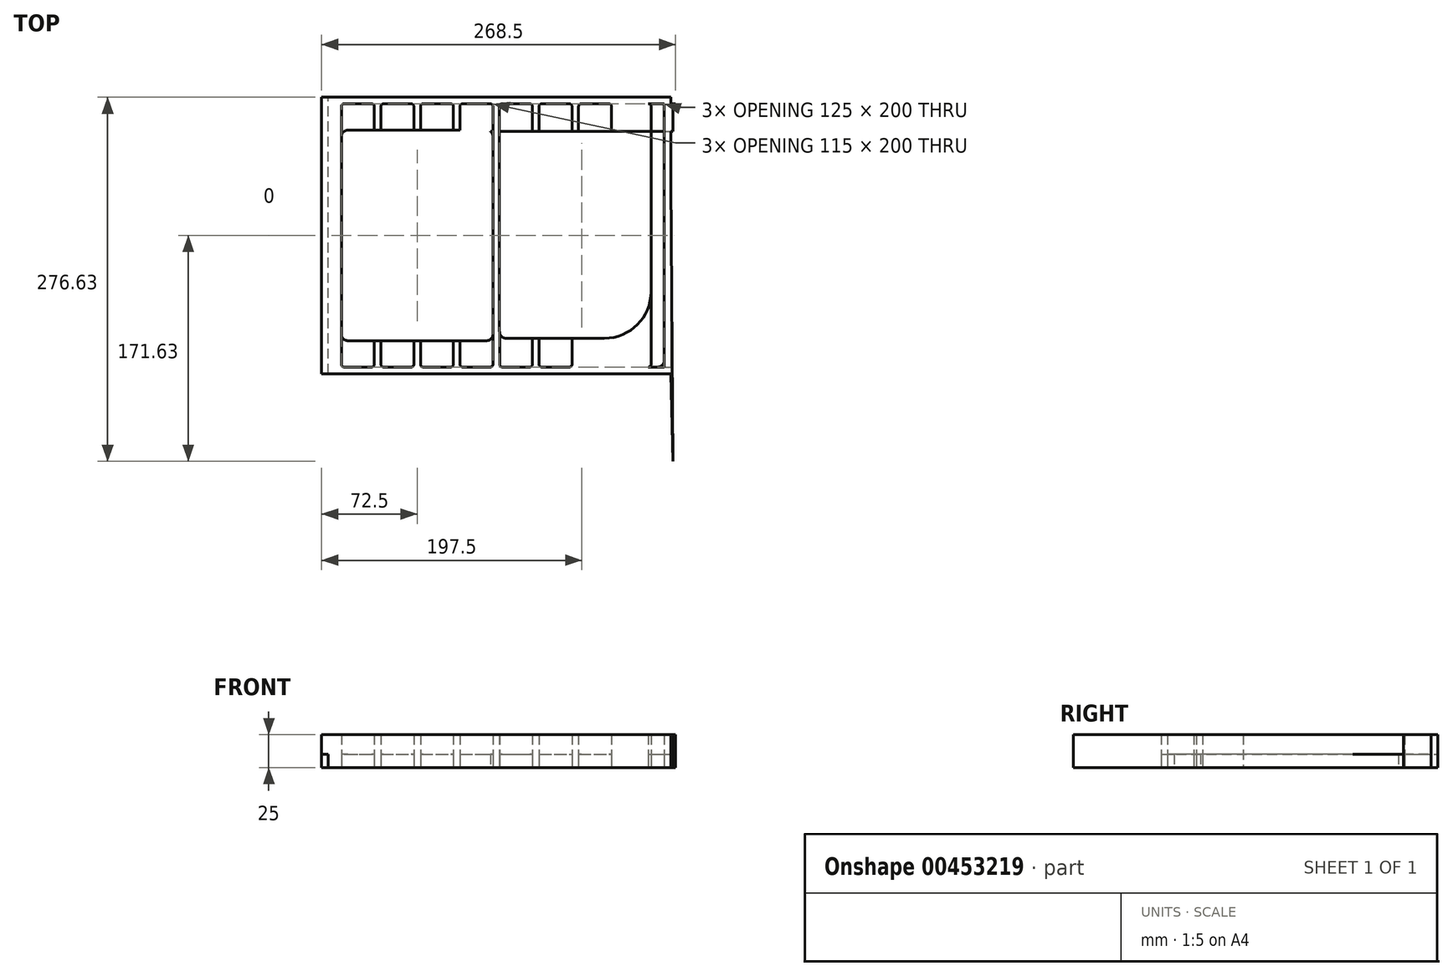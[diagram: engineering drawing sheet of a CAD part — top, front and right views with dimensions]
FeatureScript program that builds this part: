
annotation { "Feature Type Name" : "Feature", "Feature Type Description" : "" }
export const myFeature = defineFeature(function(context is Context, id is Id, definition is map)
    precondition{}
    {
        {
            var Q0;
            Q0=qCreatedBy(makeId("Top.planeOp"),FACE);
            var sketch = newSketch(context, id + "F0", { "sketchPlane" : qUnion([Q0])});
            skLineSegment(sketch, "E0.bottom", {"start": v(132.5, 105) * mm, "end": v(-132.5, 105) * mm});
            skLineSegment(sketch, "E0.top", {"start": v(132.5, -105) * mm, "end": v(-132.5, -105) * mm});
            skLineSegment(sketch, "E0.left", {"start": v(132.5, 105) * mm, "end": v(132.5, -105) * mm});
            skLineSegment(sketch, "E0.right", {"start": v(-132.5, 105) * mm, "end": v(-132.5, -105) * mm});
            skPoint(sketch, "E0.middle", {"position": v(0, 0) * mm});
            skLineSegment(sketch, "E1", {"start": v(-127.5, 95) * mm, "end": v(-127.5, -95) * mm});
            skLineSegment(sketch, "E2", {"start": v(0, 111.23) * mm, "end": v(0, -100) * mm, "construction": true});
            skPoint(sketch, "E2.endSnap0", {"position": v(0, -105) * mm});
            skLineSegment(sketch, "E3", {"start": v(-62.5, -80) * mm, "end": v(-62.5, -98) * mm});
            skLineSegment(sketch, "E4", {"start": v(-2.5, 75) * mm, "end": v(-2.5, -75) * mm});
            skLineSegment(sketch, "E5", {"start": v(2.5, 107.2) * mm, "end": v(2.5, -73.12) * mm});
            skLineSegment(sketch, "E6", {"start": v(-117.5, 75) * mm, "end": v(-117.5, -75) * mm});
            skLineSegment(sketch, "E7", {"start": v(27.5, 98) * mm, "end": v(27.5, 78.96) * mm});
            skLineSegment(sketch, "E8", {"start": v(57.5, 98) * mm, "end": v(57.5, 78.96) * mm});
            skLineSegment(sketch, "E9", {"start": v(87.5, 98) * mm, "end": v(87.5, 78.96) * mm});
            skLineSegment(sketch, "E10", {"start": v(117.5, 107.2) * mm, "end": v(117.5, -42.8) * mm});
            skLineSegment(sketch, "E11", {"start": v(32.5, 98) * mm, "end": v(32.5, 78.96) * mm});
            skLineSegment(sketch, "E12", {"start": v(62.5, 98) * mm, "end": v(62.5, 78.96) * mm});
            skLineSegment(sketch, "E13", {"start": v(134, 98) * mm, "end": v(134, 78.96) * mm});
            skLineSegment(sketch, "E14", {"start": v(127.5, 95) * mm, "end": v(127.5, -95) * mm});
            skLineSegment(sketch, "E15", {"start": v(-85.5, 100) * mm, "end": v(-64.5, 100) * mm});
            skLineSegment(sketch, "E16", {"start": v(-112.5, 80) * mm, "end": v(-7.5, 80) * mm});
            skLineSegment(sketch, "E17", {"start": v(-25.74, 78.96) * mm, "end": v(134, 78.96) * mm});
            skLineSegment(sketch, "E18", {"start": v(115.5, -100) * mm, "end": v(136, -100) * mm});
            skLineSegment(sketch, "E19", {"start": v(-112.5, -80) * mm, "end": v(-7.5, -80) * mm});
            skLineSegment(sketch, "E20", {"start": v(7.5, -78.12) * mm, "end": v(82.17, -78.12) * mm});
            skArc(sketch, "E21.filletArc", {"start": v(-112.5, 80) * mm, "mid": v(-116.04, 78.54) * mm, "end": v(-117.5, 75) * mm});
            skArc(sketch, "E22.filletArc", {"start": v(-117.5, -75) * mm, "mid": v(-116.04, -78.54) * mm, "end": v(-112.5, -80) * mm});
            skPoint(sketch, "E23.newPointB", {"position": v(-2.5, -72.8) * mm});
            skArc(sketch, "E23.filletArc", {"start": v(-7.5, -80) * mm, "mid": v(-3.96, -78.54) * mm, "end": v(-2.5, -75) * mm});
            skPoint(sketch, "E24.newPointB", {"position": v(-2.5, 137.2) * mm});
            skArc(sketch, "E24.filletArc", {"start": v(-2.5, 75) * mm, "mid": v(-3.96, 78.54) * mm, "end": v(-7.5, 80) * mm});
            skArc(sketch, "E25.filletArc", {"start": v(-25.74, 78.96) * mm, "mid": v(-29.57, 79.22) * mm, "end": v(-33.33, 80) * mm});
            skArc(sketch, "E26.filletArc", {"start": v(2.5, -73.12) * mm, "mid": v(3.96, -76.66) * mm, "end": v(7.5, -78.12) * mm});
            skArc(sketch, "E27.filletArc", {"start": v(82.17, -78.12) * mm, "mid": v(107.15, -67.77) * mm, "end": v(117.5, -42.8) * mm});
            skLineSegment(sketch, "E28.trimOffspring", {"start": v(-92.5, -80) * mm, "end": v(-92.5, -98) * mm});
            skLineSegment(sketch, "E29.trimOffspring", {"start": v(-87.5, -80) * mm, "end": v(-87.5, -98) * mm});
            skLineSegment(sketch, "E30.trimOffspring", {"start": v(-57.5, -80) * mm, "end": v(-57.5, -98) * mm});
            skLineSegment(sketch, "E31.trimOffspring", {"start": v(-32.5, -80) * mm, "end": v(-32.5, -98) * mm});
            skLineSegment(sketch, "E32.trimOffspring", {"start": v(-27.5, -80) * mm, "end": v(-27.5, -98) * mm});
            skLineSegment(sketch, "E33", {"start": v(-117.5, 100) * mm, "end": v(-122.5, 100) * mm});
            skLineSegment(sketch, "E34.trimOffspring", {"start": v(27.5, -78.12) * mm, "end": v(27.5, -98) * mm});
            skLineSegment(sketch, "E35.trimOffspring", {"start": v(32.5, -78.12) * mm, "end": v(32.5, -98) * mm});
            skLineSegment(sketch, "E36.trimOffspring", {"start": v(57.5, -78.12) * mm, "end": v(57.5, -98) * mm});
            skLineSegment(sketch, "E37.trimOffspring", {"start": v(62.5, -78.12) * mm, "end": v(62.5, -98) * mm});
            skLineSegment(sketch, "E38.trimOffspring", {"start": v(87.5, -78.12) * mm, "end": v(87.5, -98) * mm});
            skLineSegment(sketch, "E39.trimOffspring", {"start": v(134, -78.12) * mm, "end": v(134, -98) * mm});
            skLineSegment(sketch, "E40", {"start": v(-117.5, -100) * mm, "end": v(-122.5, -100) * mm});
            skLineSegment(sketch, "E41", {"start": v(117.5, -100) * mm, "end": v(122.5, -100) * mm});
            skLineSegment(sketch, "E42", {"start": v(117.5, 100) * mm, "end": v(122.5, 100) * mm});
            skLineSegment(sketch, "E43", {"start": v(2.5, 98) * mm, "end": v(2.5, 107.2) * mm});
            skLineSegment(sketch, "E44", {"start": v(-2.5, 75) * mm, "end": v(-2.5, 98) * mm});
            skLineSegment(sketch, "E45", {"start": v(-117.5, 75) * mm, "end": v(-117.5, 98) * mm});
            skLineSegment(sketch, "E46", {"start": v(-117.5, -75) * mm, "end": v(-117.5, -98) * mm});
            skLineSegment(sketch, "E47", {"start": v(-92.5, 98) * mm, "end": v(-92.5, 80) * mm});
            skLineSegment(sketch, "E48", {"start": v(-87.5, 98) * mm, "end": v(-87.5, 80) * mm});
            skLineSegment(sketch, "E49", {"start": v(-62.5, 98) * mm, "end": v(-62.5, 80) * mm});
            skLineSegment(sketch, "E50", {"start": v(-57.5, 98) * mm, "end": v(-57.5, 80) * mm});
            skLineSegment(sketch, "E51", {"start": v(-32.5, 98) * mm, "end": v(-32.5, 80) * mm});
            skLineSegment(sketch, "E52", {"start": v(-27.5, 98) * mm, "end": v(-27.5, 80) * mm});
            skLineSegment(sketch, "E53", {"start": v(117.5, 98) * mm, "end": v(117.5, 107.2) * mm});
            skLineSegment(sketch, "E54", {"start": v(117.5, -42.8) * mm, "end": v(117.5, -98) * mm});
            skPoint(sketch, "E55.visualSharp", {"position": v(-117.5, 100) * mm});
            skArc(sketch, "E55.filletArc", {"start": v(-115.5, 100) * mm, "mid": v(-116.91, 99.41) * mm, "end": v(-117.5, 98) * mm});
            skArc(sketch, "E56.filletArc", {"start": v(-127.5, -95) * mm, "mid": v(-126.04, -98.54) * mm, "end": v(-122.5, -100) * mm});
            skArc(sketch, "E57.filletArc", {"start": v(-122.5, 100) * mm, "mid": v(-126.04, 98.54) * mm, "end": v(-127.5, 95) * mm});
            skArc(sketch, "E58.filletArc", {"start": v(-85.5, 100) * mm, "mid": v(-86.91, 99.41) * mm, "end": v(-87.5, 98) * mm});
            skArc(sketch, "E59.filletArc", {"start": v(-62.5, 98) * mm, "mid": v(-63.09, 99.41) * mm, "end": v(-64.5, 100) * mm});
            skLineSegment(sketch, "E60", {"start": v(-115.5, 100) * mm, "end": v(-94.5, 100) * mm});
            skLineSegment(sketch, "E61", {"start": v(-55.5, 100) * mm, "end": v(-34.5, 100) * mm});
            skLineSegment(sketch, "E62", {"start": v(-25.5, 100) * mm, "end": v(-4.5, 100) * mm});
            skLineSegment(sketch, "E63", {"start": v(4.5, 100) * mm, "end": v(25.5, 100) * mm});
            skLineSegment(sketch, "E64", {"start": v(34.5, 100) * mm, "end": v(55.5, 100) * mm});
            skLineSegment(sketch, "E65", {"start": v(64.5, 100) * mm, "end": v(85.5, 100) * mm});
            skPoint(sketch, "E66.visualSharp", {"position": v(-57.5, 100) * mm});
            skArc(sketch, "E66.filletArc", {"start": v(-55.5, 100) * mm, "mid": v(-56.91, 99.41) * mm, "end": v(-57.5, 98) * mm});
            skPoint(sketch, "E67.visualSharp", {"position": v(-32.5, 100) * mm});
            skArc(sketch, "E67.filletArc", {"start": v(-32.5, 98) * mm, "mid": v(-33.09, 99.41) * mm, "end": v(-34.5, 100) * mm});
            skPoint(sketch, "E68.visualSharp", {"position": v(-27.5, 100) * mm});
            skArc(sketch, "E68.filletArc", {"start": v(-25.5, 100) * mm, "mid": v(-26.91, 99.41) * mm, "end": v(-27.5, 98) * mm});
            skPoint(sketch, "E69.visualSharp", {"position": v(-2.5, 100) * mm});
            skArc(sketch, "E69.filletArc", {"start": v(-2.5, 98) * mm, "mid": v(-3.09, 99.41) * mm, "end": v(-4.5, 100) * mm});
            skPoint(sketch, "E70.visualSharp", {"position": v(27.5, 100) * mm});
            skArc(sketch, "E70.filletArc", {"start": v(27.5, 98) * mm, "mid": v(26.91, 99.41) * mm, "end": v(25.5, 100) * mm});
            skPoint(sketch, "E71.visualSharp", {"position": v(2.5, 100) * mm});
            skArc(sketch, "E71.filletArc", {"start": v(4.5, 100) * mm, "mid": v(3.09, 99.41) * mm, "end": v(2.5, 98) * mm});
            skPoint(sketch, "E72.visualSharp", {"position": v(32.5, 100) * mm});
            skArc(sketch, "E72.filletArc", {"start": v(34.5, 100) * mm, "mid": v(33.09, 99.41) * mm, "end": v(32.5, 98) * mm});
            skPoint(sketch, "E73.visualSharp", {"position": v(57.5, 100) * mm});
            skArc(sketch, "E73.filletArc", {"start": v(57.5, 98) * mm, "mid": v(56.91, 99.41) * mm, "end": v(55.5, 100) * mm});
            skPoint(sketch, "E74.visualSharp", {"position": v(-92.5, 100) * mm});
            skArc(sketch, "E74.filletArc", {"start": v(-92.5, 98) * mm, "mid": v(-93.09, 99.41) * mm, "end": v(-94.5, 100) * mm});
            skPoint(sketch, "E75.visualSharp", {"position": v(62.5, 100) * mm});
            skArc(sketch, "E75.filletArc", {"start": v(64.5, 100) * mm, "mid": v(63.09, 99.41) * mm, "end": v(62.5, 98) * mm});
            skPoint(sketch, "E76.visualSharp", {"position": v(87.5, 100) * mm});
            skArc(sketch, "E76.filletArc", {"start": v(87.5, 98) * mm, "mid": v(86.91, 99.41) * mm, "end": v(85.5, 100) * mm});
            skLineSegment(sketch, "E77", {"start": v(115.5, 100) * mm, "end": v(136, 100) * mm});
            skPoint(sketch, "E78.visualSharp", {"position": v(117.5, 100) * mm});
            skArc(sketch, "E78.filletArc", {"start": v(117.5, 98) * mm, "mid": v(116.91, 99.41) * mm, "end": v(115.5, 100) * mm});
            skPoint(sketch, "E79.visualSharp", {"position": v(134, 100) * mm});
            skArc(sketch, "E79.filletArc", {"start": v(136, 100) * mm, "mid": v(134.58, 99.41) * mm, "end": v(134, 98) * mm});
            skArc(sketch, "E80.filletArc", {"start": v(127.5, 95) * mm, "mid": v(126.04, 98.54) * mm, "end": v(122.5, 100) * mm});
            skArc(sketch, "E81.filletArc", {"start": v(122.5, -100) * mm, "mid": v(126.04, -98.54) * mm, "end": v(127.5, -95) * mm});
            skPoint(sketch, "E82.visualSharp", {"position": v(117.5, -100) * mm});
            skArc(sketch, "E82.filletArc", {"start": v(115.5, -100) * mm, "mid": v(116.91, -99.41) * mm, "end": v(117.5, -98) * mm});
            skArc(sketch, "E83.filletArc", {"start": v(134, -98) * mm, "mid": v(134.58, -99.41) * mm, "end": v(136, -100) * mm});
            skLineSegment(sketch, "E84", {"start": v(-115.5, -100) * mm, "end": v(-94.5, -100) * mm});
            skLineSegment(sketch, "E85", {"start": v(-85.5, -100) * mm, "end": v(-64.5, -100) * mm});
            skLineSegment(sketch, "E86", {"start": v(-55.5, -100) * mm, "end": v(-34.5, -100) * mm});
            skPoint(sketch, "E87.end.orphan", {"position": v(0, -98.74) * mm});
            skPoint(sketch, "E88.end.orphan", {"position": v(-2.5, -98.74) * mm});
            skLineSegment(sketch, "E89", {"start": v(-25.5, -100) * mm, "end": v(-4.5, -100) * mm});
            skLineSegment(sketch, "E90", {"start": v(2.5, -73.12) * mm, "end": v(2.52, -73.6) * mm});
            skPoint(sketch, "E90.endSnap0", {"position": v(3.96, -76.66) * mm});
            skPoint(sketch, "E91.end.orphan", {"position": v(-27.5, -90) * mm});
            skPoint(sketch, "E91.start.orphan", {"position": v(-1.25, -86.87) * mm});
            skPoint(sketch, "E92.trimOffspring.end.orphan", {"position": v(3.96, -105) * mm});
            skLineSegment(sketch, "E93", {"start": v(2.52, -73.6) * mm, "end": v(2.52, -98) * mm});
            skLineSegment(sketch, "E94", {"start": v(-2.5, -75) * mm, "end": v(-2.5, -98) * mm});
            skLineSegment(sketch, "E95", {"start": v(34.5, -100) * mm, "end": v(55.5, -100) * mm});
            skLineSegment(sketch, "E96", {"start": v(64.5, -100) * mm, "end": v(85.5, -100) * mm});
            skLineSegment(sketch, "E97", {"start": v(-127.5, 95) * mm, "end": v(-127.5, 105) * mm});
            skLineSegment(sketch, "E98", {"start": v(-127.5, -95) * mm, "end": v(-127.5, -105) * mm});
            skLineSegment(sketch, "E99", {"start": v(127.5, 95) * mm, "end": v(127.5, 105) * mm});
            skLineSegment(sketch, "E100", {"start": v(127.5, -95) * mm, "end": v(127.5, -105) * mm});
            skPoint(sketch, "E101.visualSharp", {"position": v(-117.5, -100) * mm});
            skArc(sketch, "E101.filletArc", {"start": v(-117.5, -98) * mm, "mid": v(-116.91, -99.41) * mm, "end": v(-115.5, -100) * mm});
            skPoint(sketch, "E102.visualSharp", {"position": v(-92.5, -100) * mm});
            skArc(sketch, "E102.filletArc", {"start": v(-94.5, -100) * mm, "mid": v(-93.09, -99.41) * mm, "end": v(-92.5, -98) * mm});
            skPoint(sketch, "E103.visualSharp", {"position": v(-87.5, -100) * mm});
            skArc(sketch, "E103.filletArc", {"start": v(-87.5, -98) * mm, "mid": v(-86.91, -99.41) * mm, "end": v(-85.5, -100) * mm});
            skPoint(sketch, "E104.visualSharp", {"position": v(-57.5, -100) * mm});
            skArc(sketch, "E104.filletArc", {"start": v(-57.5, -98) * mm, "mid": v(-56.91, -99.41) * mm, "end": v(-55.5, -100) * mm});
            skPoint(sketch, "E105.visualSharp", {"position": v(-27.5, -100) * mm});
            skArc(sketch, "E105.filletArc", {"start": v(-27.5, -98) * mm, "mid": v(-26.91, -99.41) * mm, "end": v(-25.5, -100) * mm});
            skPoint(sketch, "E106.visualSharp", {"position": v(-62.5, -100) * mm});
            skArc(sketch, "E106.filletArc", {"start": v(-64.5, -100) * mm, "mid": v(-63.09, -99.41) * mm, "end": v(-62.5, -98) * mm});
            skPoint(sketch, "E107.visualSharp", {"position": v(-32.5, -100) * mm});
            skArc(sketch, "E107.filletArc", {"start": v(-34.5, -100) * mm, "mid": v(-33.09, -99.41) * mm, "end": v(-32.5, -98) * mm});
            skLineSegment(sketch, "E108.trimOffspring", {"start": v(0, -105) * mm, "end": v(0, -113.3) * mm, "construction": true});
            skLineSegment(sketch, "E109.trimOffspring", {"start": v(4.52, -100) * mm, "end": v(25.5, -100) * mm});
            skPoint(sketch, "E110.visualSharp", {"position": v(-2.5, -100) * mm});
            skArc(sketch, "E110.filletArc", {"start": v(-4.5, -100) * mm, "mid": v(-3.09, -99.41) * mm, "end": v(-2.5, -98) * mm});
            skPoint(sketch, "E111.visualSharp", {"position": v(57.5, -100) * mm});
            skArc(sketch, "E111.filletArc", {"start": v(55.5, -100) * mm, "mid": v(56.91, -99.41) * mm, "end": v(57.5, -98) * mm});
            skPoint(sketch, "E112.visualSharp", {"position": v(2.52, -100) * mm});
            skArc(sketch, "E112.filletArc", {"start": v(2.52, -98) * mm, "mid": v(3.1, -99.41) * mm, "end": v(4.52, -100) * mm});
            skPoint(sketch, "E113.visualSharp", {"position": v(27.5, -100) * mm});
            skArc(sketch, "E113.filletArc", {"start": v(25.5, -100) * mm, "mid": v(26.91, -99.41) * mm, "end": v(27.5, -98) * mm});
            skPoint(sketch, "E114.visualSharp", {"position": v(32.5, -100) * mm});
            skArc(sketch, "E114.filletArc", {"start": v(32.5, -98) * mm, "mid": v(33.09, -99.41) * mm, "end": v(34.5, -100) * mm});
            skPoint(sketch, "E115.visualSharp", {"position": v(62.5, -100) * mm});
            skArc(sketch, "E115.filletArc", {"start": v(62.5, -98) * mm, "mid": v(63.09, -99.41) * mm, "end": v(64.5, -100) * mm});
            skPoint(sketch, "E116.visualSharp", {"position": v(87.5, -100) * mm});
            skArc(sketch, "E116.filletArc", {"start": v(85.5, -100) * mm, "mid": v(86.91, -99.41) * mm, "end": v(87.5, -98) * mm});
            skLineSegment(sketch, "E117", {"start": v(132.5, 40.63) * mm, "end": v(132.5, 105) * mm});
            skLineSegment(sketch, "E118", {"start": v(132.5, 40.63) * mm, "end": v(134, -171.63) * mm});
            skLineSegment(sketch, "E119", {"start": v(134, -171.63) * mm, "end": v(132.5, -105) * mm});
            skArc(sketch, "E120.trimOffspring", {"start": v(-53.05, 100) * mm, "mid": v(-53.6, 102.48) * mm, "end": v(-53.9, 105) * mm});
            skSolve(sketch);
        }
        {
            var Q0;
            Q0=qCreatedBy(makeId("Front.planeOp"),FACE);
            var sketch = newSketch(context, id + "F1", { "sketchPlane" : qUnion([Q0])});
            skSolve(sketch);
        }
        {
            var Q0;
            Q0=qCreatedBy(makeId("Top.planeOp"),FACE);
            var sketch = newSketch(context, id + "F2", { "sketchPlane" : qUnion([Q0])});
            skSolve(sketch);
        }
        {
            var Q0;
            {var subQ1=sQuery(id+"F0.wireOp",EDGE,"E34.trimOffspring");Q0=makeQuery(id+"F0.imprint","IMPRINT",FACE,{"disambiguationData":[TD([[makeQuery(id+"F0.imprint","IMPRINT",EDGE,{"derivedFrom":subQ1}),-1.0]])]});}
            var Q1;
            Q1=makeQuery(id+"F0.imprint","IMPRINT",FACE,{"disambiguationData":[TD([[makeQuery(id+"F0.imprint","IMPRINT",EDGE,{"derivedFrom":sQuery(id+"F0.wireOp",EDGE,"E15")}),-1.0]])]});
            var Q2;
            {var subQ1=sQuery(id+"F0.wireOp",EDGE,"E50");Q2=makeQuery(id+"F0.imprint","IMPRINT",FACE,{"disambiguationData":[TD([[makeQuery(id+"F0.imprint","IMPRINT",EDGE,{"derivedFrom":subQ1}),1.0]])]});}
            var Q3;
            {var subQ1=sQuery(id+"F0.wireOp",EDGE,"E24.filletArc");Q3=makeQuery(id+"F0.imprint","IMPRINT",FACE,{"disambiguationData":[TD([[makeQuery(id+"F0.imprint","IMPRINT",EDGE,{"derivedFrom":subQ1}),-1.0]])]});}
            var Q4;
            {var subQ2=sQuery(id+"F0.wireOp",EDGE,"E7");Q4=makeQuery(id+"F0.imprint","IMPRINT",FACE,{"disambiguationData":[TD([[makeQuery(id+"F0.imprint","IMPRINT",EDGE,{"derivedFrom":subQ2}),-1.0]])]});}
            var Q5;
            {var subQ1=sQuery(id+"F0.wireOp",EDGE,"E8");Q5=makeQuery(id+"F0.imprint","IMPRINT",FACE,{"disambiguationData":[TD([[makeQuery(id+"F0.imprint","IMPRINT",EDGE,{"derivedFrom":subQ1}),-1.0]])]});}
            var Q6;
            {var subQ1=sQuery(id+"F0.wireOp",EDGE,"E9");Q6=makeQuery(id+"F0.imprint","IMPRINT",FACE,{"disambiguationData":[TD([[makeQuery(id+"F0.imprint","IMPRINT",EDGE,{"derivedFrom":subQ1}),-1.0]])]});}
            var Q7;
            {var subQ2=sQuery(id+"F0.wireOp",EDGE,"E13");Q7=makeQuery(id+"F0.imprint","IMPRINT",FACE,{"disambiguationData":[TD([[makeQuery(id+"F0.imprint","IMPRINT",EDGE,{"derivedFrom":subQ2}),1.0]])]});}
            var Q8;
            {var subQ0=sQuery(id+"F0.wireOp",EDGE,"E22.filletArc");Q8=makeQuery(id+"F0.imprint","IMPRINT",FACE,{"disambiguationData":[TD([[makeQuery(id+"F0.imprint","IMPRINT",EDGE,{"derivedFrom":subQ0}),-1.0]])]});}
            var Q9;
            {var subQ0=sQuery(id+"F0.wireOp",EDGE,"E3");Q9=makeQuery(id+"F0.imprint","IMPRINT",FACE,{"disambiguationData":[TD([[makeQuery(id+"F0.imprint","IMPRINT",EDGE,{"derivedFrom":subQ0}),-1.0]])]});}
            var Q10;
            {var subQ0=sQuery(id+"F0.wireOp",EDGE,"E30.trimOffspring");Q10=makeQuery(id+"F0.imprint","IMPRINT",FACE,{"disambiguationData":[TD([[makeQuery(id+"F0.imprint","IMPRINT",EDGE,{"derivedFrom":subQ0}),1.0]])]});}
            var Q11;
            {var subQ3=sQuery(id+"F0.wireOp",EDGE,"E23.filletArc");Q11=makeQuery(id+"F0.imprint","IMPRINT",FACE,{"disambiguationData":[TD([[makeQuery(id+"F0.imprint","IMPRINT",EDGE,{"derivedFrom":subQ3}),-1.0]])]});}
            var Q12;
            {var subQ0=sQuery(id+"F0.wireOp",EDGE,"E35.trimOffspring");Q12=makeQuery(id+"F0.imprint","IMPRINT",FACE,{"disambiguationData":[TD([[makeQuery(id+"F0.imprint","IMPRINT",EDGE,{"derivedFrom":subQ0}),1.0]])]});}
            var Q13;
            {var subQ0=sQuery(id+"F0.wireOp",EDGE,"E37.trimOffspring");Q13=makeQuery(id+"F0.imprint","IMPRINT",FACE,{"disambiguationData":[TD([[makeQuery(id+"F0.imprint","IMPRINT",EDGE,{"derivedFrom":subQ0}),1.0]])]});}
            var Q14;
            Q14=makeQuery(id+"F0.imprint","IMPRINT",FACE,{"disambiguationData":[TD([[makeQuery(id+"F0.imprint","IMPRINT",EDGE,{"derivedFrom":sQuery(id+"F0.wireOp",EDGE,"E18")}),1.0]])]});
            var Q15;
            {var subQ1=sQuery(id+"F0.wireOp",EDGE,"E0.right");Q15=makeQuery(id+"F0.imprint","IMPRINT",FACE,{"disambiguationData":[TD([[makeQuery(id+"F0.imprint","IMPRINT",EDGE,{"derivedFrom":subQ1}),1.0]])]});}
            var Q16;
            {var subQ0=sQuery(id+"F0.wireOp",EDGE,"E0.left");Q16=makeQuery(id+"F0.imprint","IMPRINT",FACE,{"disambiguationData":[TD([[makeQuery(id+"F0.imprint","IMPRINT",EDGE,{"derivedFrom":subQ0}),-1.0]])]});}
            var Q17;
            {var subQ1=sQuery(id+"F0.wireOp",EDGE,"E21.filletArc");Q17=makeQuery(id+"F0.imprint","IMPRINT",FACE,{"disambiguationData":[TD([[makeQuery(id+"F0.imprint","IMPRINT",EDGE,{"derivedFrom":subQ1}),-1.0]])]});}
            var Q18;
            Q18 = qSketchRegion(id + "F1", true);
            extrude(context, id + "F3", {"entities" : qUnion([Q0, Q1, Q2, Q3, Q4, Q5, Q6, Q7, Q8, Q9, Q10, Q11, Q12, Q13, Q14, Q15, Q16, Q17, Q18]), "depth" : 10 * mm});
        }
        {
            var Q0;
            Q0=qCreatedBy(makeId("Top.planeOp"),FACE);
            var sketch = newSketch(context, id + "F4", { "sketchPlane" : qUnion([Q0])});
            skSolve(sketch);
        }
        {
            var Q0;
            Q0 = qSketchRegion(id + "F0", true);
            extrude(context, id + "F5", {"entities" : qUnion([Q0]), "depth" : 25 * mm});
        }
        {
            var Q0;
            Q0 = qSketchRegion(id + "F4", true);
            var Q1;
            Q1 = qSketchRegion(id + "F0", true);
            var Q2;
            Q2 = qSketchRegion(id + "F2", true);
            extrude(context, id + "F6", {"entities" : qUnion([Q0, Q1, Q2]), "depth" : 25 * mm});
        }
        {
            var Q0;
            Q0 = qSketchRegion(id + "F0", true);
            extrude(context, id + "F7", {"entities" : qUnion([Q0]), "depth" : 25 * mm});
        }
    });
